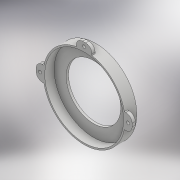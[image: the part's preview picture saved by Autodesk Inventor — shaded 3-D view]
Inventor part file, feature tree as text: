
AUTODESK INVENTOR PART (.ipt)
format: ipt  version: 2017 (Build 210142000, 142)  size: 196,096 bytes
history: native  units: mm
features: extrude x3, sketch x3, fillet x1, projected_geometry x1
ambient origin geometry x8: Origin, YZ Plane, XZ Plane, XY Plane, X Axis, Y Axis, Z Axis, Center Point
bodies: Solid1 (feature_tree)
feature tree (8):
  extrude  "Extrusion1"  Depth=52.5mm
  extrude  "Extrusion2"  Depth=7.5mm
  extrude  "Extrusion3"  Depth=4.0mm
  fillet  "Fillet1"  Radius=0.5mm
  sketch  "Sketch1"  dims[d0=50.5mm d1=52.5mm]
  sketch  "Sketch2"  dims[d2=7.5mm d3=0.0mm d4=35.0mm]
  projected_geometry  "Projected Loop1"
  sketch  "Sketch3"  dims[d5=1.5mm d6=0.0mm d7=0.5mm d8=0.5mm d9=0.5mm d10=5.0mm d11=5.0mm d12=10.0mm d13=5.0mm d14=180.0deg d15=5.0mm d16=10.0mm d17=5.0mm d18=90.0deg d19=5.0mm d20=90.0deg d21=5.0mm d22=10.0mm d23=90.0deg d24=2.0mm d25=2.0mm d26=2.0mm d27=2.0mm d28=0.0mm d29=4.0mm]
